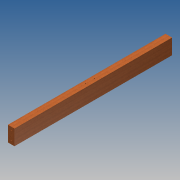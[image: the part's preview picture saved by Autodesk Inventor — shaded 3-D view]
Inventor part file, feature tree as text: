
AUTODESK INVENTOR PART (.ipt)
format: ipt  version: 2014 SP1 (Build 180222100, 222)  size: 102,912 bytes
history: native  units: in
note: dims shown in document units (in); Inventor stores cm internally (conversion verified against a paired STEP export)
features: sketch x4, hole x3, extrude x1
ambient origin geometry x8: Origin, YZ Plane, XZ Plane, XY Plane, X Axis, Y Axis, Z Axis, Center Point
bodies: Solid1 (feature_tree)
feature tree (8):
  extrude  "Extrusion1"  Depth=3.5in
  hole  "Hole2"  [1 undecoded]
  hole  "Hole3"  [1 undecoded]
  hole  "Hole4"  [1 undecoded]
  sketch  "Sketch1"  dims[d0=1.5in d1=3.5in]
  sketch  "Sketch3"  dims[d2=36.0in d3=0.0in d21=0.75in]
  sketch  "Sketch4"  dims[d22=0.7874in d24=2.0in d25=0.3937in d27=1.0in]
  sketch  "Sketch5"  dims[d29=0.201in d30=0.75in d31=0.385in d32=0.25in d33=0.5635in d34=1.0in d35=0.8108in d36=0.75in d37=0.7874in d39=2.0in d40=0.3937in d42=1.0in d44=0.201in d45=0.75in d46=0.385in d47=0.25in d48=0.5635in d49=1.0in d50=0.8108in d51=1.0in d52=0.201in d53=0.75in d54=0.385in d55=0.25in d56=0.5635in d57=1.0in d58=0.8108in]
note: 3 required parameter values undecoded (feature->parameter linkage not recoverable at this tier; creation-order binding heuristic only, values carry confidence <= 0.55)
